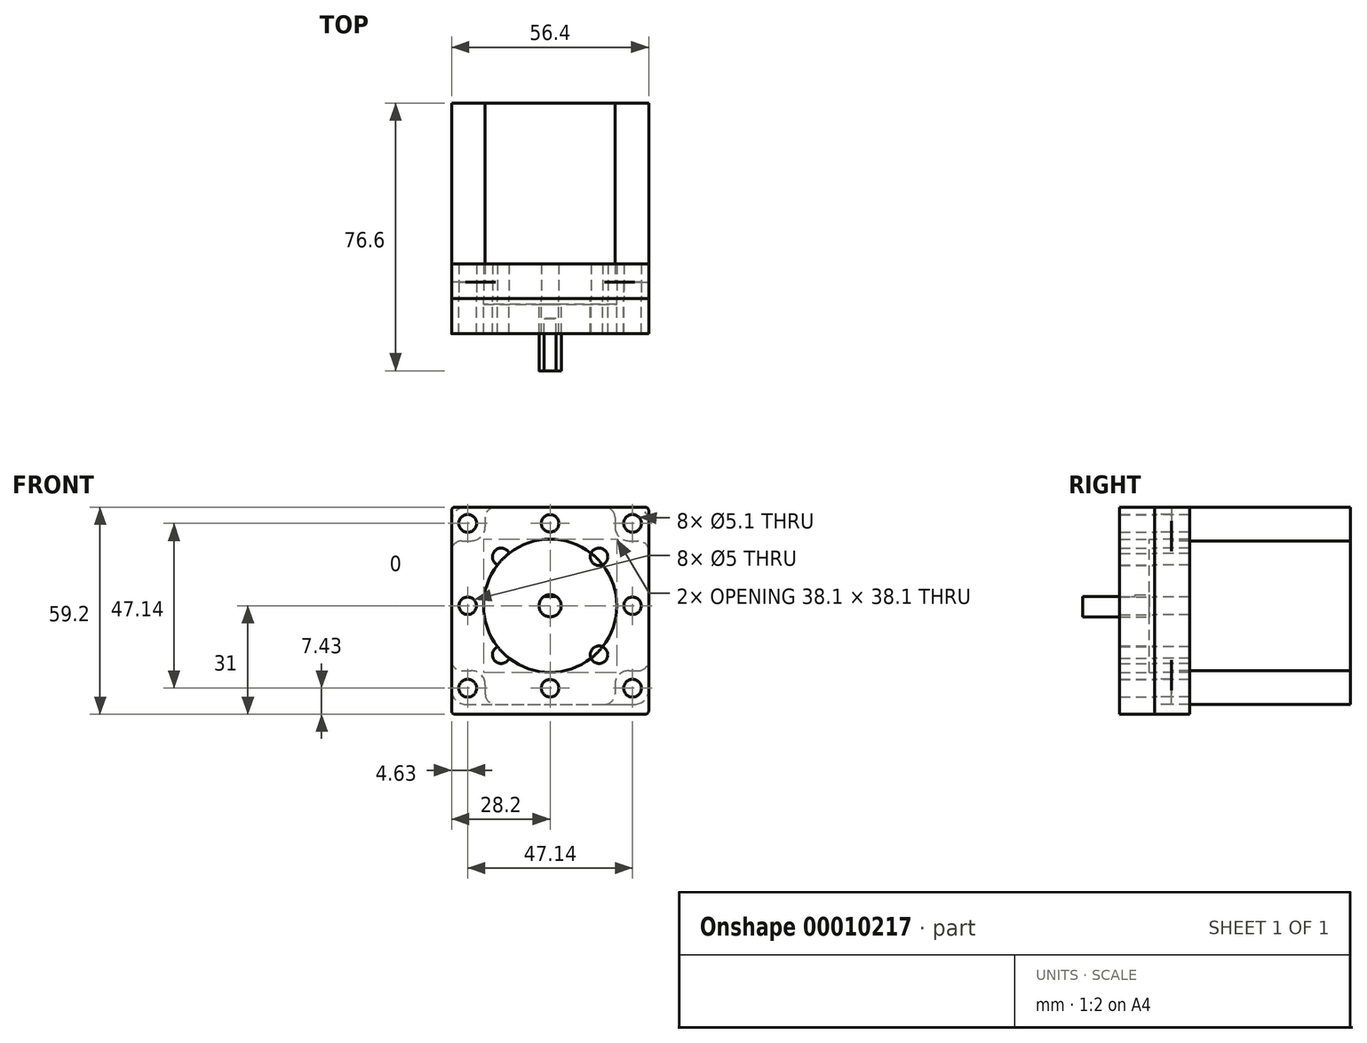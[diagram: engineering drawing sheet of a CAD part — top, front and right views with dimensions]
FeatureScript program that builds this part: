
annotation { "Feature Type Name" : "Feature", "Feature Type Description" : "" }
export const myFeature = defineFeature(function(context is Context, id is Id, definition is map)
    precondition{}
    {
        {
            var Q0;
            Q0=qCreatedBy(makeId("Front.planeOp"),FACE);
            var sketch = newSketch(context, id + "F0", { "sketchPlane" : qUnion([Q0])});
            skLineSegment(sketch, "E0.rect.bottom", {"start": v(-28.2, 28.2) * mm, "end": v(28.2, 28.2) * mm});
            skLineSegment(sketch, "E0.rect.top", {"start": v(-28.2, -28.2) * mm, "end": v(28.2, -28.2) * mm});
            skLineSegment(sketch, "E0.rect.left", {"start": v(-28.2, 28.2) * mm, "end": v(-28.2, -28.2) * mm});
            skLineSegment(sketch, "E0.rect.right", {"start": v(28.2, 28.2) * mm, "end": v(28.2, -28.2) * mm});
            skPoint(sketch, "E0.rect.middle", {"position": v(0, 0) * mm});
            skCircle(sketch, "E1", {"center": v(0, 0) * mm, "radius": 19.05 * mm});
            skCircle(sketch, "E2", {"center": v(0, 0) * mm, "radius": 3.17 * mm});
            skCircle(sketch, "E3", {"center": v(-23.57, 23.57) * mm, "radius": 2.55 * mm});
            skCircle(sketch, "E4", {"center": v(23.57, 23.57) * mm, "radius": 2.55 * mm});
            skCircle(sketch, "E5", {"center": v(23.57, -23.57) * mm, "radius": 2.55 * mm});
            skCircle(sketch, "E6", {"center": v(-23.57, -23.57) * mm, "radius": 2.55 * mm});
            skLineSegment(sketch, "E7.rect.bottom", {"start": v(-23.57, 23.57) * mm, "end": v(23.57, 23.57) * mm, "construction": true});
            skLineSegment(sketch, "E7.rect.top", {"start": v(-23.57, -23.57) * mm, "end": v(23.57, -23.57) * mm, "construction": true});
            skLineSegment(sketch, "E7.rect.left", {"start": v(-23.57, 23.57) * mm, "end": v(-23.57, -23.57) * mm, "construction": true});
            skLineSegment(sketch, "E7.rect.right", {"start": v(23.57, 23.57) * mm, "end": v(23.57, -23.57) * mm, "construction": true});
            skSolve(sketch);
        }
        {
            var Q0;
            Q0=makeQuery(id+"F0.imprint","IMPRINT",FACE,{"disambiguationData":[TD([[makeQuery(id+"F0.imprint","IMPRINT",EDGE,{"derivedFrom":sQuery(id+"F0.wireOp",EDGE,"E0.rect.bottom")}),-1.0]])]});
            var Q1;
            Q1=makeQuery(id+"F0.imprint","IMPRINT",FACE,{"disambiguationData":[TD([[makeQuery(id+"F0.imprint","IMPRINT",EDGE,{"derivedFrom":sQuery(id+"F0.wireOp",EDGE,"E1")}),1.0]])]});
            var Q2;
            Q2=makeQuery(id+"F0.imprint","IMPRINT",FACE,{"disambiguationData":[TD([[makeQuery(id+"F0.imprint","IMPRINT",EDGE,{"derivedFrom":sQuery(id+"F0.wireOp",EDGE,"E2")}),1.0]])]});
            extrude(context, id + "F1", {"entities" : qUnion([Q0, Q1, Q2]), "oppositeDirection" : true, "depth" : 4.8 * mm});
        }
        {
            var Q0;
            Q0=makeQuery(id+"F0.imprint","IMPRINT",FACE,{"disambiguationData":[TD([[makeQuery(id+"F0.imprint","IMPRINT",EDGE,{"derivedFrom":sQuery(id+"F0.wireOp",EDGE,"E1")}),1.0]])]});
            extrude(context, id + "F2", {"entities" : qUnion([Q0]), "operationType" : NewBodyOperationType.ADD, "depth" : 1.6 * mm});
        }
        {
            var Q0;
            Q0=makeQuery(id+"F0.imprint","IMPRINT",FACE,{"disambiguationData":[TD([[makeQuery(id+"F0.imprint","IMPRINT",EDGE,{"derivedFrom":sQuery(id+"F0.wireOp",EDGE,"E2")}),1.0]])]});
            extrude(context, id + "F3", {"entities" : qUnion([Q0]), "operationType" : NewBodyOperationType.ADD, "depth" : 20.6 * mm});
        }
        {
            var Q0;
            Q0=makeQuery(id+"F1.opExtrude","SWEPT_EDGE",EDGE,{"disambiguationData":[OSD([sQuery(id+"F0.wireOp",EDGE,"E0.rect.bottom"),sQuery(id+"F0.wireOp",EDGE,"E0.rect.left")])]});
            var Q1;
            Q1=makeQuery(id+"F1.opExtrude","SWEPT_EDGE",EDGE,{"disambiguationData":[OSD([sQuery(id+"F0.wireOp",EDGE,"E0.rect.bottom"),sQuery(id+"F0.wireOp",EDGE,"E0.rect.right")])]});
            var Q2;
            Q2=makeQuery(id+"F1.opExtrude","SWEPT_EDGE",EDGE,{"disambiguationData":[OSD([sQuery(id+"F0.wireOp",EDGE,"E0.rect.top"),sQuery(id+"F0.wireOp",EDGE,"E0.rect.right")])]});
            var Q3;
            Q3=makeQuery(id+"F1.opExtrude","SWEPT_EDGE",EDGE,{"disambiguationData":[OSD([sQuery(id+"F0.wireOp",EDGE,"E0.rect.top"),sQuery(id+"F0.wireOp",EDGE,"E0.rect.left")])]});
            fillet(context, id + "F4", {"entities" : qUnion([Q0, Q1, Q2, Q3]), "radius" : 4 * mm, "tangentPropagation" : true, "allowEdgeOverflow" : false});
        }
        {
            var Q0;
            Q0=makeQuery(id+"F1.opExtrude","SWEPT_FACE",FACE,{"disambiguationData":[OSD([sQuery(id+"F0.wireOp",EDGE,"E0.rect.left")])]});
            var sketch = newSketch(context, id + "F5", { "sketchPlane" : qUnion([Q0])});
            skLineSegment(sketch, "E8", {"start": v(1.6, 3.17) * mm, "end": v(20.6, 3.17) * mm});
            skLineSegment(sketch, "E9.0", {"start": v(20.6, 3.17) * mm, "end": v(20.6, -3.17) * mm});
            skLineSegment(sketch, "E10", {"start": v(5.6, 3.17) * mm, "end": v(5.6, 2.67) * mm});
            skLineSegment(sketch, "E11", {"start": v(5.6, 2.67) * mm, "end": v(20.6, 2.67) * mm});
            skSolve(sketch);
        }
        {
            var Q0;
            {var subQ1=sQuery(id+"F5.wireOp",EDGE,"E10");Q0=makeQuery(id+"F5.imprint","IMPRINT",FACE,{"disambiguationData":[TD([[makeQuery(id+"F5.imprint","IMPRINT",EDGE,{"derivedFrom":subQ1}),1.0]])]});}
            extrude(context, id + "F6", {"entities" : qUnion([Q0]), "operationType" : NewBodyOperationType.REMOVE, "endBound" : BoundingType.THROUGH_ALL, "oppositeDirection" : true, "depth" : 25 * mm});
        }
        {
            var Q0;
            Q0=qCreatedBy(makeId("Front.planeOp"),FACE);
            var sketch = newSketch(context, id + "F7", { "sketchPlane" : qUnion([Q0])});
            skPoint(sketch, "E12.rect.middle", {"position": v(0, 0.02) * mm});
            skPoint(sketch, "E13", {"position": v(0, 0) * mm});
            skLineSegment(sketch, "E14.rect.bottom", {"start": v(-18.57, 28.2) * mm, "end": v(18.57, 28.2) * mm});
            skLineSegment(sketch, "E14.rect.top", {"start": v(-18.57, -28.2) * mm, "end": v(18.57, -28.2) * mm});
            skLineSegment(sketch, "E14.rect.left", {"start": v(-18.57, 28.2) * mm, "end": v(-18.57, -28.2) * mm});
            skLineSegment(sketch, "E14.rect.right", {"start": v(18.57, 28.2) * mm, "end": v(18.57, -28.2) * mm});
            skLineSegment(sketch, "E15.rect.bottom", {"start": v(-28.2, 18.57) * mm, "end": v(28.2, 18.57) * mm});
            skLineSegment(sketch, "E15.rect.top", {"start": v(-28.2, -18.57) * mm, "end": v(28.2, -18.57) * mm});
            skLineSegment(sketch, "E15.rect.left", {"start": v(-28.2, 18.57) * mm, "end": v(-28.2, -18.57) * mm});
            skLineSegment(sketch, "E15.rect.right", {"start": v(28.2, 18.57) * mm, "end": v(28.2, -18.57) * mm});
            skSolve(sketch);
        }
        {
            var Q0;
            Q0=qSketchRegion(id+"F7",true);
            extrude(context, id + "F8", {"entities" : qUnion([Q0]), "operationType" : NewBodyOperationType.ADD, "oppositeDirection" : true, "depth" : 56 * mm});
        }
        {
            var Q0;
            Q0=makeQuery(id+"F8.opExtrude","SWEPT_EDGE",EDGE,{"disambiguationData":[OSD([sQuery(id+"F7.wireOp",EDGE,"E14.rect.right"),sQuery(id+"F7.wireOp",EDGE,"E15.rect.bottom")])]});
            var Q1;
            Q1=makeQuery(id+"F8.opExtrude","SWEPT_EDGE",EDGE,{"disambiguationData":[OSD([sQuery(id+"F7.wireOp",EDGE,"E14.rect.left"),sQuery(id+"F7.wireOp",EDGE,"E15.rect.bottom")])]});
            var Q2;
            Q2=makeQuery(id+"F8.opExtrude","SWEPT_EDGE",EDGE,{"disambiguationData":[OSD([sQuery(id+"F7.wireOp",EDGE,"E14.rect.left"),sQuery(id+"F7.wireOp",EDGE,"E15.rect.top")])]});
            var Q3;
            Q3=makeQuery(id+"F8.opExtrude","SWEPT_EDGE",EDGE,{"disambiguationData":[OSD([sQuery(id+"F7.wireOp",EDGE,"E14.rect.right"),sQuery(id+"F7.wireOp",EDGE,"E15.rect.top")])]});
            fillet(context, id + "F9", {"entities" : qUnion([Q0, Q1, Q2, Q3]), "radius" : 4 * mm, "tangentPropagation" : true, "allowEdgeOverflow" : false});
        }
        {
            var Q0;
            Q0=makeQuery(id+"F8.opExtrude","SWEPT_EDGE",EDGE,{"disambiguationData":[OSD([sQuery(id+"F7.wireOp",EDGE,"E14.rect.bottom"),sQuery(id+"F7.wireOp",EDGE,"E14.rect.right")])]});
            var Q1;
            Q1=makeQuery(id+"F8.opExtrude","SWEPT_EDGE",EDGE,{"disambiguationData":[OSD([sQuery(id+"F7.wireOp",EDGE,"E15.rect.bottom"),sQuery(id+"F7.wireOp",EDGE,"E15.rect.right")])]});
            var Q2;
            Q2=makeQuery(id+"F8.opExtrude","SWEPT_EDGE",EDGE,{"disambiguationData":[OSD([sQuery(id+"F7.wireOp",EDGE,"E15.rect.top"),sQuery(id+"F7.wireOp",EDGE,"E15.rect.right")])]});
            var Q3;
            Q3=makeQuery(id+"F8.opExtrude","SWEPT_EDGE",EDGE,{"disambiguationData":[OSD([sQuery(id+"F7.wireOp",EDGE,"E14.rect.top"),sQuery(id+"F7.wireOp",EDGE,"E14.rect.right")])]});
            var Q4;
            Q4=makeQuery(id+"F8.opExtrude","SWEPT_EDGE",EDGE,{"disambiguationData":[OSD([sQuery(id+"F7.wireOp",EDGE,"E14.rect.top"),sQuery(id+"F7.wireOp",EDGE,"E14.rect.left")])]});
            var Q5;
            Q5=makeQuery(id+"F8.opExtrude","SWEPT_EDGE",EDGE,{"disambiguationData":[OSD([sQuery(id+"F7.wireOp",EDGE,"E15.rect.top"),sQuery(id+"F7.wireOp",EDGE,"E15.rect.left")])]});
            var Q6;
            Q6=makeQuery(id+"F8.opExtrude","SWEPT_EDGE",EDGE,{"disambiguationData":[OSD([sQuery(id+"F7.wireOp",EDGE,"E15.rect.bottom"),sQuery(id+"F7.wireOp",EDGE,"E15.rect.left")])]});
            var Q7;
            Q7=makeQuery(id+"F8.opExtrude","SWEPT_EDGE",EDGE,{"disambiguationData":[OSD([sQuery(id+"F7.wireOp",EDGE,"E14.rect.bottom"),sQuery(id+"F7.wireOp",EDGE,"E14.rect.left")])]});
            fillet(context, id + "F10", {"entities" : qUnion([Q0, Q1, Q2, Q3, Q4, Q5, Q6, Q7]), "radius" : 3 * mm, "tangentPropagation" : true, "allowEdgeOverflow" : false});
        }
        {
            var Q0;
            Q0=qCreatedBy(makeId("Front.planeOp"),FACE);
            var sketch = newSketch(context, id + "F11", { "sketchPlane" : qUnion([Q0])});
            skLineSegment(sketch, "E16", {"start": v(-35, -31) * mm, "end": v(35, -31) * mm});
            skLineSegment(sketch, "E17", {"start": v(35, -31) * mm, "end": v(35, -21) * mm});
            skLineSegment(sketch, "E18", {"start": v(35, -21) * mm, "end": v(20, -21) * mm});
            skLineSegment(sketch, "E19", {"start": v(20, -21) * mm, "end": v(20, 20) * mm});
            skLineSegment(sketch, "E20", {"start": v(20, 20) * mm, "end": v(-20, 20) * mm});
            skLineSegment(sketch, "E21", {"start": v(-20, 20) * mm, "end": v(-20, -21.67) * mm});
            skLineSegment(sketch, "E22", {"start": v(-20, -21.67) * mm, "end": v(-35, -21.67) * mm});
            skLineSegment(sketch, "E23", {"start": v(-35, -21.67) * mm, "end": v(-35, -31) * mm});
            skLineSegment(sketch, "E24", {"start": v(0, 50.48) * mm, "end": v(0, -37.63) * mm, "construction": true});
            skLineSegment(sketch, "E25", {"start": v(-35.93, 0) * mm, "end": v(34.56, 0) * mm, "construction": true});
            skCircle(sketch, "E26", {"center": v(0, 0) * mm, "radius": 15 * mm});
            skCircle(sketch, "E27", {"center": v(0, 0) * mm, "radius": 13 * mm});
            skLineSegment(sketch, "E28", {"start": v(-14, 38.33) * mm, "end": v(-14, -25.13) * mm, "construction": true});
            skLineSegment(sketch, "E29.MirrorCS", {"start": v(14, 38.33) * mm, "end": v(14, -25.13) * mm, "construction": true});
            skLineSegment(sketch, "E30", {"start": v(31.89, 14) * mm, "end": v(-14, 14) * mm, "construction": true});
            skLineSegment(sketch, "E31.MirrorCS", {"start": v(31.89, -14) * mm, "end": v(-14, -14) * mm, "construction": true});
            skCircle(sketch, "E32", {"center": v(-14, 14) * mm, "radius": 2.5 * mm});
            skCircle(sketch, "E33", {"center": v(14, 14) * mm, "radius": 2.5 * mm});
            skCircle(sketch, "E34", {"center": v(-14, -14) * mm, "radius": 2.5 * mm});
            skCircle(sketch, "E35", {"center": v(14, -14) * mm, "radius": 2.5 * mm});
            skSolve(sketch);
        }
        {
            var Q0;
            Q0=qCreatedBy(makeId("Front.planeOp"),FACE);
            var sketch = newSketch(context, id + "F12", { "sketchPlane" : qUnion([Q0])});
            skLineSegment(sketch, "E36.0", {"start": v(-28.2, 28.2) * mm, "end": v(28.2, 28.2) * mm});
            skLineSegment(sketch, "E37.0", {"start": v(-28.2, 28.2) * mm, "end": v(-28.2, -28.2) * mm, "construction": true});
            skLineSegment(sketch, "E38.0", {"start": v(28.2, 28.2) * mm, "end": v(28.2, -28.2) * mm, "construction": true});
            skLineSegment(sketch, "E39.0", {"start": v(-35, -31) * mm, "end": v(35, -31) * mm, "construction": true});
            skCircle(sketch, "E40.0", {"center": v(-23.57, 23.57) * mm, "radius": 2.55 * mm});
            skCircle(sketch, "E41.0", {"center": v(23.57, 23.57) * mm, "radius": 2.55 * mm});
            skCircle(sketch, "E42.0", {"center": v(23.57, -23.57) * mm, "radius": 2.55 * mm});
            skCircle(sketch, "E43.0", {"center": v(-23.57, -23.57) * mm, "radius": 2.55 * mm});
            skCircle(sketch, "E44.0", {"center": v(-14, -14) * mm, "radius": 2.5 * mm});
            skCircle(sketch, "E45.0", {"center": v(-14, 14) * mm, "radius": 2.5 * mm});
            skCircle(sketch, "E46.0", {"center": v(14, 14) * mm, "radius": 2.5 * mm});
            skCircle(sketch, "E47.0", {"center": v(14, -14) * mm, "radius": 2.5 * mm});
            skPoint(sketch, "E48.0", {"position": v(0, 0) * mm});
            skCircle(sketch, "E49.0", {"center": v(0, 0) * mm, "radius": 15 * mm});
            skCircle(sketch, "E50.0", {"center": v(0, 0) * mm, "radius": 19.05 * mm});
            skLineSegment(sketch, "E51", {"start": v(-28.2, 28.2) * mm, "end": v(-28.2, -31) * mm});
            skLineSegment(sketch, "E52", {"start": v(-28.2, -31) * mm, "end": v(28.2, -31) * mm});
            skLineSegment(sketch, "E53", {"start": v(28.2, -31) * mm, "end": v(28.2, 28.2) * mm});
            skLineSegment(sketch, "E54", {"start": v(-23.57, 23.57) * mm, "end": v(-23.57, -23.57) * mm, "construction": true});
            skLineSegment(sketch, "E55", {"start": v(-23.57, -23.57) * mm, "end": v(23.57, -23.57) * mm, "construction": true});
            skLineSegment(sketch, "E56", {"start": v(23.57, -23.57) * mm, "end": v(23.57, 23.57) * mm, "construction": true});
            skLineSegment(sketch, "E57", {"start": v(23.57, 23.57) * mm, "end": v(-23.57, 23.57) * mm, "construction": true});
            skCircle(sketch, "E58", {"center": v(0, 23.57) * mm, "radius": 2.5 * mm});
            skCircle(sketch, "E59", {"center": v(23.57, 0) * mm, "radius": 2.5 * mm});
            skCircle(sketch, "E60", {"center": v(0, -23.57) * mm, "radius": 2.5 * mm});
            skCircle(sketch, "E61", {"center": v(-23.57, 0) * mm, "radius": 2.5 * mm});
            skSolve(sketch);
        }
        {
            var Q0;
            Q0=makeQuery(id+"F12.imprint","IMPRINT",FACE,{"disambiguationData":[TD([[makeQuery(id+"F12.imprint","IMPRINT",EDGE,{"derivedFrom":sQuery(id+"F12.wireOp",EDGE,"E36.0")}),-1.0]])]});
            var Q1;
            Q1=makeQuery(id+"F12.imprint","IMPRINT",FACE,{"disambiguationData":[TD([[makeQuery(id+"F12.imprint","IMPRINT",EDGE,{"derivedFrom":sQuery(id+"F12.wireOp",EDGE,"E49.0")}),-1.0]])]});
            var Q2;
            Q2=makeQuery(id+"F12.imprint","IMPRINT",FACE,{"disambiguationData":[TD([[makeQuery(id+"F12.imprint","IMPRINT",EDGE,{"derivedFrom":sQuery(id+"F12.wireOp",EDGE,"E40.0")}),1.0]])]});
            var Q3;
            Q3=makeQuery(id+"F12.imprint","IMPRINT",FACE,{"disambiguationData":[TD([[makeQuery(id+"F12.imprint","IMPRINT",EDGE,{"derivedFrom":sQuery(id+"F12.wireOp",EDGE,"E41.0")}),1.0]])]});
            var Q4;
            Q4=makeQuery(id+"F12.imprint","IMPRINT",FACE,{"disambiguationData":[TD([[makeQuery(id+"F12.imprint","IMPRINT",EDGE,{"derivedFrom":sQuery(id+"F12.wireOp",EDGE,"E42.0")}),1.0]])]});
            var Q5;
            Q5=makeQuery(id+"F12.imprint","IMPRINT",FACE,{"disambiguationData":[TD([[makeQuery(id+"F12.imprint","IMPRINT",EDGE,{"derivedFrom":sQuery(id+"F12.wireOp",EDGE,"E43.0")}),1.0]])]});
            extrude(context, id + "F13", {"entities" : qUnion([Q0, Q1, Q2, Q3, Q4, Q5]), "oppositeDirection" : true, "depth" : 10 * mm});
        }
        {
            var Q0;
            Q0=makeQuery(id+"F12.imprint","IMPRINT",FACE,{"disambiguationData":[TD([[makeQuery(id+"F12.imprint","IMPRINT",EDGE,{"derivedFrom":sQuery(id+"F12.wireOp",EDGE,"E36.0")}),-1.0]])]});
            var Q1;
            {var subQ0=sQuery(id+"F12.wireOp",EDGE,"E50.0");var subQ1=sQuery(id+"F12.wireOp",EDGE,"E45.0");var subQ3=makeQuery(id+"F12.imprint","INTERSECT",VERTEX,{"disambiguationData":[OD(0.0)],"derivedFrom":[subQ1,subQ0]});Q1=makeQuery(id+"F12.imprint","IMPRINT",FACE,{"disambiguationData":[TD([[makeQuery(id+"F12.imprint","IMPRINT",EDGE,{"disambiguationData":[TD([[subQ3,-1.0]])],"derivedFrom":subQ1}),1.0]])]});}
            var Q2;
            {var subQ0=sQuery(id+"F12.wireOp",EDGE,"E50.0");var subQ1=sQuery(id+"F12.wireOp",EDGE,"E46.0");var subQ3=makeQuery(id+"F12.imprint","INTERSECT",VERTEX,{"disambiguationData":[OD(0.0)],"derivedFrom":[subQ1,subQ0]});Q2=makeQuery(id+"F12.imprint","IMPRINT",FACE,{"disambiguationData":[TD([[makeQuery(id+"F12.imprint","IMPRINT",EDGE,{"disambiguationData":[TD([[subQ3,1.0]])],"derivedFrom":subQ1}),1.0]])]});}
            var Q3;
            {var subQ0=sQuery(id+"F12.wireOp",EDGE,"E50.0");var subQ1=sQuery(id+"F12.wireOp",EDGE,"E47.0");var subQ3=makeQuery(id+"F12.imprint","INTERSECT",VERTEX,{"disambiguationData":[OD(0.0)],"derivedFrom":[subQ1,subQ0]});Q3=makeQuery(id+"F12.imprint","IMPRINT",FACE,{"disambiguationData":[TD([[makeQuery(id+"F12.imprint","IMPRINT",EDGE,{"disambiguationData":[TD([[subQ3,-1.0]])],"derivedFrom":subQ1}),1.0]])]});}
            var Q4;
            {var subQ0=sQuery(id+"F12.wireOp",EDGE,"E50.0");var subQ1=sQuery(id+"F12.wireOp",EDGE,"E44.0");var subQ3=makeQuery(id+"F12.imprint","INTERSECT",VERTEX,{"disambiguationData":[OD(0.0)],"derivedFrom":[subQ1,subQ0]});Q4=makeQuery(id+"F12.imprint","IMPRINT",FACE,{"disambiguationData":[TD([[makeQuery(id+"F12.imprint","IMPRINT",EDGE,{"disambiguationData":[TD([[subQ3,-1.0]])],"derivedFrom":subQ1}),1.0]])]});}
            extrude(context, id + "F14", {"entities" : qUnion([Q0, Q1, Q2, Q3, Q4]), "depth" : 10 * mm});
        }
        {
            var Q0;
            Q0=makeQuery(id+"F14.opExtrude","SWEPT_EDGE",EDGE,{"disambiguationData":[OSD([sQuery(id+"F12.wireOp",EDGE,"E36.0"),sQuery(id+"F12.wireOp",EDGE,"E53")])]});
            var Q1;
            Q1=makeQuery(id+"F14.opExtrude","SWEPT_EDGE",EDGE,{"disambiguationData":[OSD([sQuery(id+"F12.wireOp",EDGE,"E52"),sQuery(id+"F12.wireOp",EDGE,"E53")])]});
            var Q2;
            Q2=makeQuery(id+"F14.opExtrude","SWEPT_EDGE",EDGE,{"disambiguationData":[OSD([sQuery(id+"F12.wireOp",EDGE,"E36.0"),sQuery(id+"F12.wireOp",EDGE,"E51")])]});
            var Q3;
            Q3=makeQuery(id+"F14.opExtrude","SWEPT_EDGE",EDGE,{"disambiguationData":[OSD([sQuery(id+"F12.wireOp",EDGE,"E51"),sQuery(id+"F12.wireOp",EDGE,"E52")])]});
            fillet(context, id + "F15", {"entities" : qUnion([Q0, Q1, Q2, Q3]), "radius" : 1 * mm, "tangentPropagation" : true, "allowEdgeOverflow" : false});
        }
        {
            var Q0;
            Q0=makeQuery(id+"F13.opExtrude","SWEPT_EDGE",EDGE,{"disambiguationData":[OSD([sQuery(id+"F12.wireOp",EDGE,"E36.0"),sQuery(id+"F12.wireOp",EDGE,"E51")])]});
            var Q1;
            Q1=makeQuery(id+"F13.opExtrude","SWEPT_EDGE",EDGE,{"disambiguationData":[OSD([sQuery(id+"F12.wireOp",EDGE,"E51"),sQuery(id+"F12.wireOp",EDGE,"E52")])]});
            var Q2;
            Q2=makeQuery(id+"F13.opExtrude","SWEPT_EDGE",EDGE,{"disambiguationData":[OSD([sQuery(id+"F12.wireOp",EDGE,"E36.0"),sQuery(id+"F12.wireOp",EDGE,"E53")])]});
            var Q3;
            Q3=makeQuery(id+"F13.opExtrude","SWEPT_EDGE",EDGE,{"disambiguationData":[OSD([sQuery(id+"F12.wireOp",EDGE,"E52"),sQuery(id+"F12.wireOp",EDGE,"E53")])]});
            fillet(context, id + "F16", {"entities" : qUnion([Q0, Q1, Q2, Q3]), "radius" : 1 * mm, "tangentPropagation" : true, "allowEdgeOverflow" : false});
        }
    });
